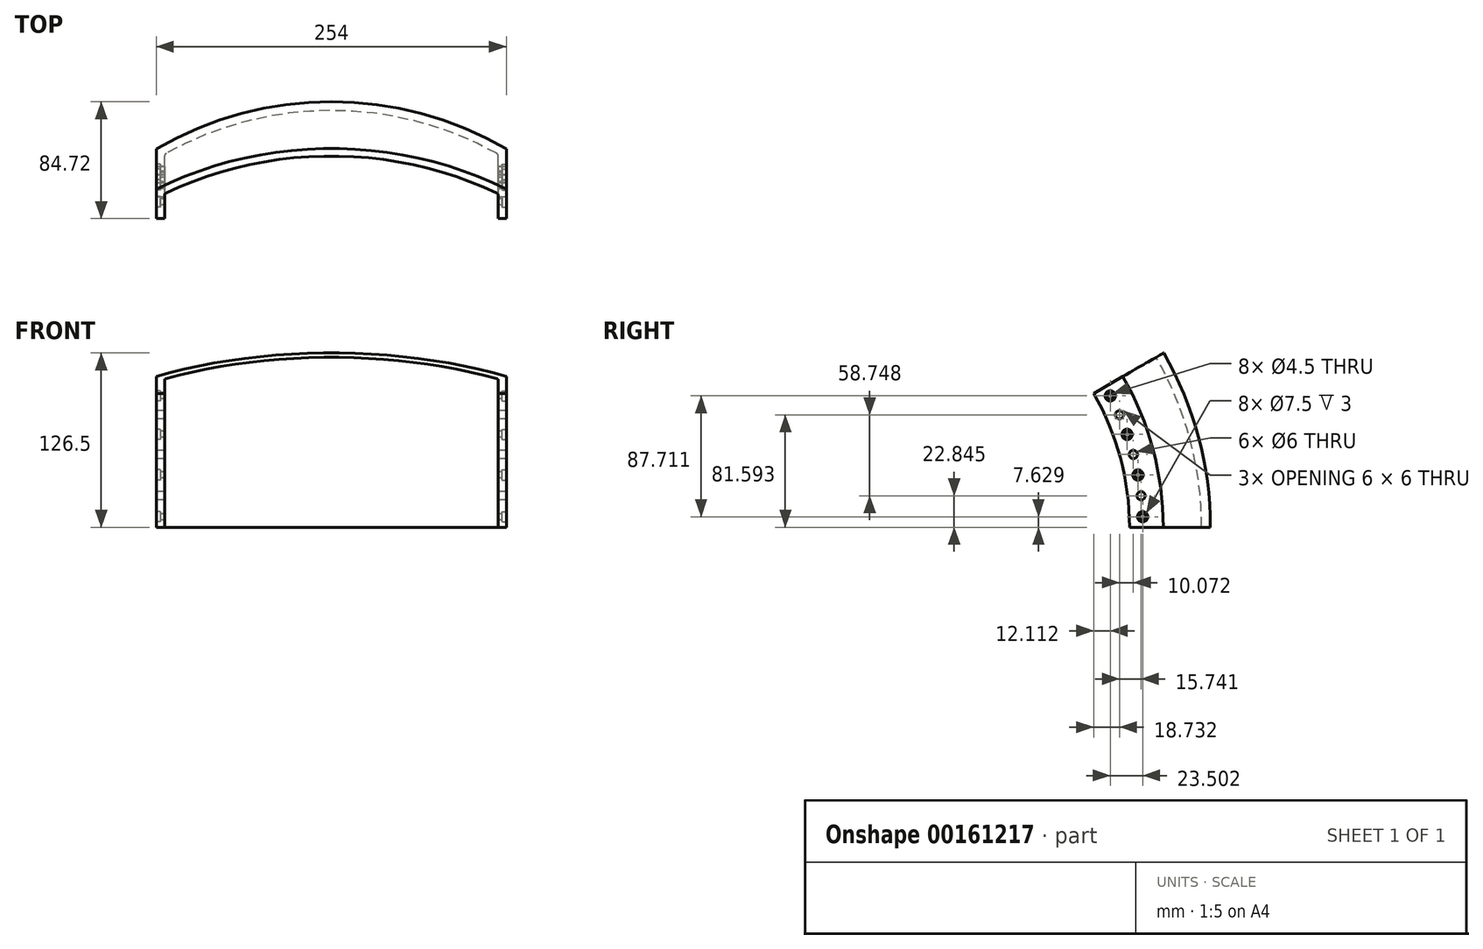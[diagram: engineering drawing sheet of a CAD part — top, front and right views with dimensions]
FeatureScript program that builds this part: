
annotation { "Feature Type Name" : "Feature", "Feature Type Description" : "" }
export const myFeature = defineFeature(function(context is Context, id is Id, definition is map)
    precondition{}
    {
        {
            var Q0;
            Q0=qCreatedBy(makeId("Top.planeOp"),FACE);
            var sketch = newSketch(context, id + "F0", { "sketchPlane" : qUnion([Q0])});
            skArc(sketch, "E0", {"start": v(127, 218.81) * mm, "mid": v(0, 253) * mm, "end": v(-127, 218.81) * mm});
            skLineSegment(sketch, "E1", {"start": v(0, 253) * mm, "end": v(127, 253) * mm, "construction": true});
            skLineSegment(sketch, "E2", {"start": v(127, 253) * mm, "end": v(127, 218.81) * mm, "construction": true});
            skLineSegment(sketch, "E3", {"start": v(127, 218.81) * mm, "end": v(127, 194.31) * mm});
            skLineSegment(sketch, "E4", {"start": v(127, 194.31) * mm, "end": v(121, 194.31) * mm});
            skLineSegment(sketch, "E5", {"start": v(121, 194.31) * mm, "end": v(121, 214.93) * mm});
            skLineSegment(sketch, "E6.MirrorCS", {"start": v(-121, 194.31) * mm, "end": v(-121, 214.93) * mm});
            skLineSegment(sketch, "E7.MirrorCS", {"start": v(-127, 218.81) * mm, "end": v(-127, 194.31) * mm});
            skLineSegment(sketch, "E8.MirrorCS", {"start": v(-127, 194.31) * mm, "end": v(-121, 194.31) * mm});
            skPoint(sketch, "E9.MirrorCS.end.orphan", {"position": v(-127, 218.81) * mm});
            skPoint(sketch, "E9.MirrorCS.start.orphan", {"position": v(-127, 253) * mm});
            skPoint(sketch, "E10.MirrorCS.start.orphan", {"position": v(0, 253) * mm});
            skLineSegment(sketch, "E11", {"start": v(0, 0) * mm, "end": v(139.33, 0) * mm, "construction": true});
            skLineSegment(sketch, "E12", {"start": v(0, 253) * mm, "end": v(0, 246.65) * mm});
            skPoint(sketch, "E13.orphan", {"position": v(121, 210.73) * mm});
            skPoint(sketch, "E14.orphan", {"position": v(-121, 210.73) * mm});
            skArc(sketch, "E15.trimOffspring", {"start": v(121, 214.93) * mm, "mid": v(0, 246.65) * mm, "end": v(-121, 214.93) * mm});
            skSolve(sketch);
        }
        {
            var Q0;
            Q0=qSketchRegion(id+"F0",true);
            var Q1;
            Q1=sQuery(id+"F0.wireOp",EDGE,"E11");
            revolve(context, id + "F1", {"entities" : qUnion([Q0]), "axis" : qUnion([Q1]), "revolveType" : RevolveType.ONE_DIRECTION, "angle" : 30 * degree});
        }
        {
            var Q0;
            Q0=makeQuery(id+"F1.opRevolve","SWEPT_EDGE",EDGE,{"disambiguationData":[OSD([sQuery(id+"F0.wireOp",EDGE,"E5"),sQuery(id+"F0.wireOp",EDGE,"E15.trimOffspring")])]});
            fillet(context, id + "F2", {"entities" : qUnion([Q0]), "radius" : 2 * mm, "tangentPropagation" : true, "allowEdgeOverflow" : false});
        }
        {
            var Q0;
            Q0=makeQuery(id+"F1.opRevolve","SWEPT_EDGE",EDGE,{"disambiguationData":[OSD([sQuery(id+"F0.wireOp",EDGE,"E6.MirrorCS"),sQuery(id+"F0.wireOp",EDGE,"E15.trimOffspring")])]});
            fillet(context, id + "F3", {"entities" : qUnion([Q0]), "radius" : 2 * mm, "tangentPropagation" : true, "allowEdgeOverflow" : false});
        }
        {
            var Q0;
            Q0=makeQuery(id+"F1.opRevolve","SWEPT_FACE",FACE,{"disambiguationData":[OSD([sQuery(id+"F0.wireOp",EDGE,"E6.MirrorCS")])]});
            var sketch = newSketch(context, id + "F4", { "sketchPlane" : qUnion([Q0])});
            skPoint(sketch, "E16", {"position": v(197.08, 52.8) * mm});
            skPoint(sketch, "E17.1.0", {"position": v(192.59, 67.39) * mm});
            skPoint(sketch, "E17.2.0", {"position": v(187.01, 81.6) * mm});
            skPoint(sketch, "E17.3.0", {"position": v(180.4, 95.34) * mm});
            skPoint(sketch, "E17.4.0", {"position": v(172.76, 108.55) * mm});
            skPoint(sketch, "E17.5.0", {"position": v(164.17, 121.16) * mm});
            skPoint(sketch, "E17.6.0", {"position": v(154.65, 133.1) * mm});
            skPoint(sketch, "E17.7.0", {"position": v(144.28, 144.28) * mm});
            skPoint(sketch, "E17.8.0", {"position": v(133.1, 154.65) * mm});
            skPoint(sketch, "E17.9.0", {"position": v(121.16, 164.17) * mm});
            skPoint(sketch, "E17.10.0", {"position": v(108.55, 172.76) * mm});
            skPoint(sketch, "E17.11.0", {"position": v(95.34, 180.4) * mm});
            skPoint(sketch, "E17.12.0", {"position": v(81.6, 187.01) * mm});
            skPoint(sketch, "E17.13.0", {"position": v(67.39, 192.59) * mm});
            skPoint(sketch, "E17.14.0", {"position": v(52.8, 197.08) * mm});
            skPoint(sketch, "E17.15.0", {"position": v(37.93, 200.48) * mm});
            skPoint(sketch, "E17.16.0", {"position": v(22.84, 202.75) * mm});
            skPoint(sketch, "E17.17.0", {"position": v(7.63, 203.9) * mm});
            skPoint(sketch, "E17.18.0", {"position": v(-7.63, 203.9) * mm});
            skPoint(sketch, "E17.19.0", {"position": v(-22.84, 202.75) * mm});
            skPoint(sketch, "E17.20.0", {"position": v(-37.93, 200.48) * mm});
            skPoint(sketch, "E17.21.0", {"position": v(-52.8, 197.08) * mm});
            skPoint(sketch, "E17.22.0", {"position": v(-67.39, 192.59) * mm});
            skPoint(sketch, "E17.23.0", {"position": v(-81.6, 187.01) * mm});
            skPoint(sketch, "E17.24.0", {"position": v(-95.34, 180.4) * mm});
            skPoint(sketch, "E17.25.0", {"position": v(-108.55, 172.76) * mm});
            skPoint(sketch, "E17.26.0", {"position": v(-121.16, 164.17) * mm});
            skPoint(sketch, "E17.27.0", {"position": v(-133.1, 154.65) * mm});
            skPoint(sketch, "E17.28.0", {"position": v(-144.28, 144.28) * mm});
            skPoint(sketch, "E17.29.0", {"position": v(-154.65, 133.1) * mm});
            skPoint(sketch, "E17.30.0", {"position": v(-164.17, 121.16) * mm});
            skPoint(sketch, "E17.31.0", {"position": v(-172.76, 108.55) * mm});
            skPoint(sketch, "E17.32.0", {"position": v(-180.4, 95.34) * mm});
            skPoint(sketch, "E17.33.0", {"position": v(-187.01, 81.6) * mm});
            skPoint(sketch, "E17.34.0", {"position": v(-192.59, 67.39) * mm});
            skPoint(sketch, "E17.35.0", {"position": v(-197.08, 52.8) * mm});
            skPoint(sketch, "E17.36.0", {"position": v(-200.48, 37.93) * mm});
            skPoint(sketch, "E17.37.0", {"position": v(-202.75, 22.84) * mm});
            skPoint(sketch, "E17.38.0", {"position": v(-203.9, 7.63) * mm});
            skPoint(sketch, "E17.39.0", {"position": v(-203.9, -7.63) * mm});
            skPoint(sketch, "E17.40.0", {"position": v(-202.75, -22.84) * mm});
            skPoint(sketch, "E17.41.0", {"position": v(-200.48, -37.93) * mm});
            skPoint(sketch, "E17.42.0", {"position": v(-197.08, -52.8) * mm});
            skPoint(sketch, "E17.43.0", {"position": v(-192.59, -67.39) * mm});
            skPoint(sketch, "E17.44.0", {"position": v(-187.01, -81.6) * mm});
            skPoint(sketch, "E17.45.0", {"position": v(-180.4, -95.34) * mm});
            skPoint(sketch, "E17.46.0", {"position": v(-172.76, -108.55) * mm});
            skPoint(sketch, "E17.47.0", {"position": v(-164.17, -121.16) * mm});
            skPoint(sketch, "E17.48.0", {"position": v(-154.65, -133.1) * mm});
            skPoint(sketch, "E17.49.0", {"position": v(-144.28, -144.28) * mm});
            skPoint(sketch, "E17.50.0", {"position": v(-133.1, -154.65) * mm});
            skPoint(sketch, "E17.51.0", {"position": v(-121.16, -164.17) * mm});
            skPoint(sketch, "E17.52.0", {"position": v(-108.55, -172.76) * mm});
            skPoint(sketch, "E17.53.0", {"position": v(-95.34, -180.4) * mm});
            skPoint(sketch, "E17.54.0", {"position": v(-81.6, -187.01) * mm});
            skPoint(sketch, "E17.55.0", {"position": v(-67.39, -192.59) * mm});
            skPoint(sketch, "E17.56.0", {"position": v(-52.8, -197.08) * mm});
            skPoint(sketch, "E17.57.0", {"position": v(-37.93, -200.48) * mm});
            skPoint(sketch, "E17.58.0", {"position": v(-22.84, -202.75) * mm});
            skPoint(sketch, "E17.59.0", {"position": v(-7.63, -203.9) * mm});
            skPoint(sketch, "E17.60.0", {"position": v(7.63, -203.9) * mm});
            skPoint(sketch, "E17.61.0", {"position": v(22.84, -202.75) * mm});
            skPoint(sketch, "E17.62.0", {"position": v(37.93, -200.48) * mm});
            skPoint(sketch, "E17.63.0", {"position": v(52.8, -197.08) * mm});
            skPoint(sketch, "E17.64.0", {"position": v(67.39, -192.59) * mm});
            skPoint(sketch, "E17.65.0", {"position": v(81.6, -187.01) * mm});
            skPoint(sketch, "E17.66.0", {"position": v(95.34, -180.4) * mm});
            skPoint(sketch, "E17.67.0", {"position": v(108.55, -172.76) * mm});
            skPoint(sketch, "E17.68.0", {"position": v(121.16, -164.17) * mm});
            skPoint(sketch, "E17.69.0", {"position": v(133.1, -154.65) * mm});
            skPoint(sketch, "E17.70.0", {"position": v(144.28, -144.28) * mm});
            skPoint(sketch, "E17.71.0", {"position": v(154.65, -133.1) * mm});
            skPoint(sketch, "E17.72.0", {"position": v(164.17, -121.16) * mm});
            skPoint(sketch, "E17.73.0", {"position": v(172.76, -108.55) * mm});
            skPoint(sketch, "E17.74.0", {"position": v(180.4, -95.34) * mm});
            skPoint(sketch, "E17.75.0", {"position": v(187.01, -81.6) * mm});
            skPoint(sketch, "E17.76.0", {"position": v(192.59, -67.39) * mm});
            skPoint(sketch, "E17.77.0", {"position": v(197.08, -52.8) * mm});
            skPoint(sketch, "E17.78.0", {"position": v(200.48, -37.93) * mm});
            skPoint(sketch, "E17.79.0", {"position": v(202.75, -22.84) * mm});
            skPoint(sketch, "E17.80.0", {"position": v(203.9, -7.63) * mm});
            skPoint(sketch, "E17.81.0", {"position": v(203.9, 7.63) * mm});
            skPoint(sketch, "E17.82.0", {"position": v(202.75, 22.84) * mm});
            skPoint(sketch, "E17.83.0", {"position": v(200.48, 37.93) * mm});
            skPoint(sketch, "E17.center", {"position": v(0, 0) * mm});
            skCircle(sketch, "E18", {"center": v(203.9, 7.63) * mm, "radius": 2.25 * mm});
            skCircle(sketch, "E19", {"center": v(202.75, 22.84) * mm, "radius": 3 * mm});
            skCircle(sketch, "E20", {"center": v(200.48, 37.93) * mm, "radius": 2.25 * mm});
            skCircle(sketch, "E21", {"center": v(197.08, 52.8) * mm, "radius": 3 * mm});
            skCircle(sketch, "E22", {"center": v(192.59, 67.39) * mm, "radius": 2.25 * mm});
            skCircle(sketch, "E23", {"center": v(187.01, 81.6) * mm, "radius": 3 * mm});
            skCircle(sketch, "E24", {"center": v(180.4, 95.34) * mm, "radius": 2.25 * mm});
            skSolve(sketch);
        }
        {
            var Q0;
            Q0=qSketchRegion(id+"F4",true);
            extrude(context, id + "F5", {"entities" : qUnion([Q0]), "operationType" : NewBodyOperationType.REMOVE, "endBound" : BoundingType.SYMMETRIC, "depth" : 848.38 * mm});
        }
        {
            var Q0;
            Q0=makeQuery(id+"F1.opRevolve","SWEPT_FACE",FACE,{"disambiguationData":[OSD([sQuery(id+"F0.wireOp",EDGE,"E3")])]});
            var sketch = newSketch(context, id + "F6", { "sketchPlane" : qUnion([Q0])});
            skCircle(sketch, "E25", {"center": v(203.9, 7.63) * mm, "radius": 3.75 * mm});
            skCircle(sketch, "E26", {"center": v(200.48, 37.93) * mm, "radius": 3.75 * mm});
            skCircle(sketch, "E27", {"center": v(192.59, 67.39) * mm, "radius": 3.75 * mm});
            skCircle(sketch, "E28", {"center": v(180.4, 95.34) * mm, "radius": 3.75 * mm});
            skSolve(sketch);
        }
        {
            var Q0;
            Q0=qSketchRegion(id+"F6",true);
            extrude(context, id + "F7", {"entities" : qUnion([Q0]), "operationType" : NewBodyOperationType.REMOVE, "oppositeDirection" : true, "depth" : 3 * mm});
        }
        {
            var Q0;
            Q0=makeQuery(id+"F1.opRevolve","SWEPT_FACE",FACE,{"disambiguationData":[OSD([sQuery(id+"F0.wireOp",EDGE,"E7.MirrorCS")])]});
            var sketch = newSketch(context, id + "F8", { "sketchPlane" : qUnion([Q0])});
            skCircle(sketch, "E29", {"center": v(-203.9, 7.63) * mm, "radius": 3.75 * mm});
            skCircle(sketch, "E30", {"center": v(-200.48, 37.93) * mm, "radius": 3.75 * mm});
            skCircle(sketch, "E31", {"center": v(-192.59, 67.39) * mm, "radius": 3.75 * mm});
            skCircle(sketch, "E32", {"center": v(-180.4, 95.34) * mm, "radius": 3.75 * mm});
            skSolve(sketch);
        }
        {
            var Q0;
            Q0=qSketchRegion(id+"F8",true);
            extrude(context, id + "F9", {"entities" : qUnion([Q0]), "operationType" : NewBodyOperationType.REMOVE, "oppositeDirection" : true, "depth" : 3 * mm});
        }
    });
